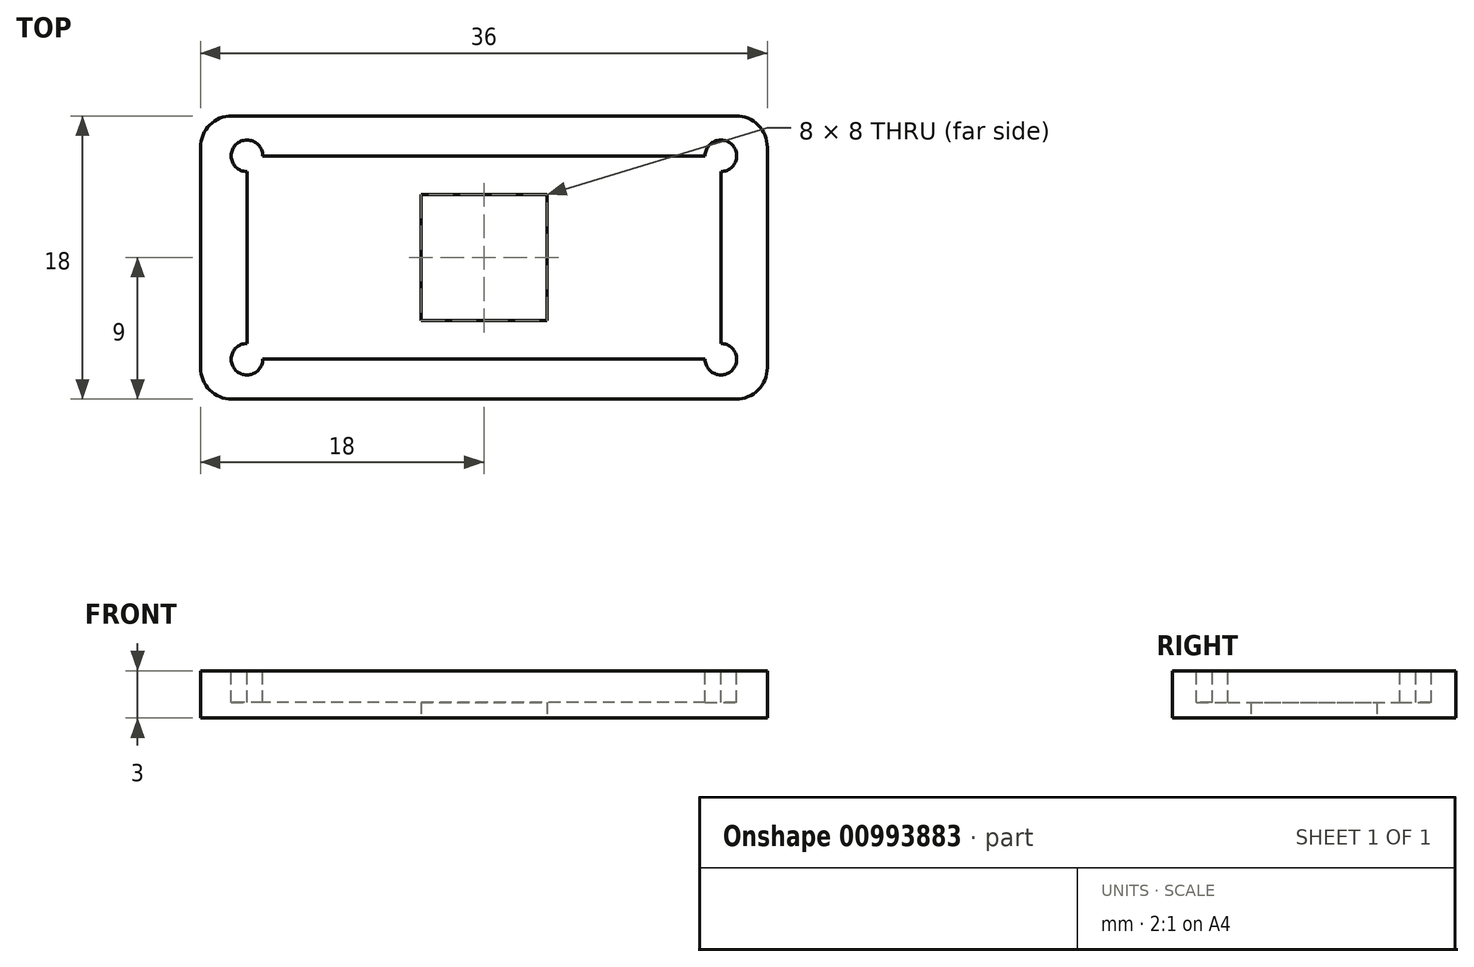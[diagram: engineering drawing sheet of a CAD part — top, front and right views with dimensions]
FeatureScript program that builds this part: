
annotation { "Feature Type Name" : "Feature", "Feature Type Description" : "" }
export const myFeature = defineFeature(function(context is Context, id is Id, definition is map)
    precondition{}
    {
        {
            var Q0;
            Q0=qCreatedBy(makeId("Top.planeOp"),FACE);
            var sketch = newSketch(context, id + "F0", { "sketchPlane" : qUnion([Q0])});
            skLineSegment(sketch, "E0.bottom", {"start": v(18, -9) * mm, "end": v(-18, -9) * mm});
            skLineSegment(sketch, "E0.top", {"start": v(18, 9) * mm, "end": v(-18, 9) * mm});
            skLineSegment(sketch, "E0.left", {"start": v(18, -9) * mm, "end": v(18, 9) * mm});
            skLineSegment(sketch, "E0.right", {"start": v(-18, -9) * mm, "end": v(-18, 9) * mm});
            skPoint(sketch, "E0.middle", {"position": v(0, 0) * mm});
            skSolve(sketch);
        }
        {
            var Q0;
            Q0=makeQuery(id+"F0.imprint","IMPRINT",FACE,{"disambiguationData":[TD([[makeQuery(id+"F0.imprint","IMPRINT",EDGE,{"derivedFrom":sQuery(id+"F0.wireOp",EDGE,"E0.bottom")}),-1.0]])]});
            extrude(context, id + "F1", {"entities" : qUnion([Q0]), "depth" : 3 * mm, "offsetDistance" : 25 * mm});
        }
        {
            var Q0;
            Q0=makeQuery(id+"F1.opExtrude","CAP_FACE",FACE,{"disambiguationData":[OSD([sQuery(id+"F0.wireOp",EDGE,"E0.bottom"),sQuery(id+"F0.wireOp",EDGE,"E0.top"),sQuery(id+"F0.wireOp",EDGE,"E0.left"),sQuery(id+"F0.wireOp",EDGE,"E0.right")])],"isStart":false});
            var sketch = newSketch(context, id + "F2", { "sketchPlane" : qUnion([Q0])});
            skLineSegment(sketch, "E1.bottom", {"start": v(15.05, -6.46) * mm, "end": v(-15.05, -6.46) * mm});
            skLineSegment(sketch, "E1.top", {"start": v(15.05, 6.46) * mm, "end": v(-15.05, 6.46) * mm});
            skLineSegment(sketch, "E1.left", {"start": v(15.05, -6.46) * mm, "end": v(15.05, 6.46) * mm});
            skLineSegment(sketch, "E1.right", {"start": v(-15.05, -6.46) * mm, "end": v(-15.05, 6.46) * mm});
            skPoint(sketch, "E1.middle", {"position": v(0, 0) * mm});
            skSolve(sketch);
        }
        {
            var Q0;
            Q0=makeQuery(id+"F2.imprint","IMPRINT",FACE,{"disambiguationData":[TD([[makeQuery(id+"F2.imprint","IMPRINT",EDGE,{"derivedFrom":sQuery(id+"F2.wireOp",EDGE,"E1.bottom")}),-1.0]])]});
            extrude(context, id + "F3", {"entities" : qUnion([Q0]), "operationType" : NewBodyOperationType.REMOVE, "oppositeDirection" : true, "depth" : 2 * mm, "offsetDistance" : 25 * mm});
        }
        {
            var Q0;
            Q0=makeQuery(id+"F1.opExtrude","CAP_FACE",FACE,{"disambiguationData":[OSD([sQuery(id+"F0.wireOp",EDGE,"E0.bottom"),sQuery(id+"F0.wireOp",EDGE,"E0.top"),sQuery(id+"F0.wireOp",EDGE,"E0.left"),sQuery(id+"F0.wireOp",EDGE,"E0.right")])],"isStart":true});
            var sketch = newSketch(context, id + "F4", { "sketchPlane" : qUnion([Q0])});
            skLineSegment(sketch, "E2.bottom", {"start": v(4, -4) * mm, "end": v(-4, -4) * mm});
            skLineSegment(sketch, "E2.top", {"start": v(4, 4) * mm, "end": v(-4, 4) * mm});
            skLineSegment(sketch, "E2.left", {"start": v(4, -4) * mm, "end": v(4, 4) * mm});
            skLineSegment(sketch, "E2.right", {"start": v(-4, -4) * mm, "end": v(-4, 4) * mm});
            skPoint(sketch, "E2.middle", {"position": v(0, 0) * mm});
            skSolve(sketch);
        }
        {
            var Q0;
            Q0=qSketchRegion(id+"F4",true);
            extrude(context, id + "F5", {"entities" : qUnion([Q0]), "operationType" : NewBodyOperationType.REMOVE, "endBound" : BoundingType.THROUGH_ALL, "oppositeDirection" : true, "depth" : 25 * mm, "offsetDistance" : 25 * mm});
        }
        {
            var Q0;
            Q0=makeQuery(id+"F1.opExtrude","SWEPT_EDGE",EDGE,{"disambiguationData":[OSD([sQuery(id+"F0.wireOp",EDGE,"E0.bottom"),sQuery(id+"F0.wireOp",EDGE,"E0.right")])]});
            var Q1;
            Q1=makeQuery(id+"F1.opExtrude","SWEPT_EDGE",EDGE,{"disambiguationData":[OSD([sQuery(id+"F0.wireOp",EDGE,"E0.top"),sQuery(id+"F0.wireOp",EDGE,"E0.right")])]});
            var Q2;
            Q2=makeQuery(id+"F1.opExtrude","SWEPT_EDGE",EDGE,{"disambiguationData":[OSD([sQuery(id+"F0.wireOp",EDGE,"E0.bottom"),sQuery(id+"F0.wireOp",EDGE,"E0.left")])]});
            var Q3;
            Q3=makeQuery(id+"F1.opExtrude","SWEPT_EDGE",EDGE,{"disambiguationData":[OSD([sQuery(id+"F0.wireOp",EDGE,"E0.top"),sQuery(id+"F0.wireOp",EDGE,"E0.left")])]});
            fillet(context, id + "F6", {"entities" : qUnion([Q0, Q1, Q2, Q3]), "radius" : 2 * mm, "tangentPropagation" : true, "allowEdgeOverflow" : false});
        }
        {
            var Q0;
            Q0=makeQuery(id+"F1.opExtrude","CAP_FACE",FACE,{"disambiguationData":[OSD([sQuery(id+"F0.wireOp",EDGE,"E0.bottom"),sQuery(id+"F0.wireOp",EDGE,"E0.top"),sQuery(id+"F0.wireOp",EDGE,"E0.left"),sQuery(id+"F0.wireOp",EDGE,"E0.right")])],"isStart":false});
            var sketch = newSketch(context, id + "F7", { "sketchPlane" : qUnion([Q0])});
            skCircle(sketch, "E3", {"center": v(-15.05, 6.46) * mm, "radius": 1 * mm});
            skCircle(sketch, "E4", {"center": v(-15.05, -6.46) * mm, "radius": 1 * mm});
            skCircle(sketch, "E5", {"center": v(15.05, 6.46) * mm, "radius": 1 * mm});
            skCircle(sketch, "E6", {"center": v(15.05, -6.46) * mm, "radius": 1 * mm});
            skSolve(sketch);
        }
        {
            var Q0;
            Q0=qSketchRegion(id+"F7",true);
            extrude(context, id + "F8", {"entities" : qUnion([Q0]), "operationType" : NewBodyOperationType.REMOVE, "oppositeDirection" : true, "depth" : 2 * mm, "offsetDistance" : 25 * mm});
        }
    });
